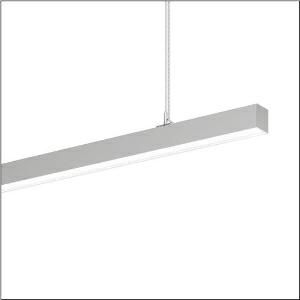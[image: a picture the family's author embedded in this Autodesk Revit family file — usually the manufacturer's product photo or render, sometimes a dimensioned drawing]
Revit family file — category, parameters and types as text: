
# Revit family: silica_r__21_51mx33da37sb_bea4
name_source: partatom
category: Lighting Fixtures
units: mm (PartAtom-declared; Revit-internal decimal feet)

## family parameters
Cut with Voids When Loaded = No
Host = Face
Light Source = No
Part Type = Normal
Room Calculation Point = No
Round Connector Dimension = Use Diameter
Shared = No

## types (1)
- --- (1 x LED, 5910 lm, 41.3 W, 3000K)
    Apparent Load = 41 VA
    CIE Flux Codes = 78 96 99 55 100
    Color Rendering = 80
    Color Temperature = 3000K
    Default Elevation = 1800 mm
    Description = Silica® 21, office luminaire, primary optical cover: prismatic diffuser, of PMMA, CAT 2 (L<= 3000cd/m²), light emission: direct/indirect distribution, primary light characteristic: symmetric, installation type: suspended mounting, LED, rated luminous flux: 5.910lm, luminous efficacy: 143lm/W, light colour: 830, colour temperature: 3000K, with terminal, 3+2-pole, max. 2.5mm², mains connection: 220..240V, AC, 50/60Hz, rated input power: 41.3W, luminaire housing, of aluminium, metallic grey (RAL 9006), length: 1.204mm, width: 53mm, height: 53mm, protection rating (complete): IP20, insulation class (complete): insulation class I (protective earthing), certification: CE, permissible operating ambient temperature: 0..+35°C, standard: EN 50419, packaging unit: 1 piece
    Height = 53 mm
    Lamp = 1 x LED
    Lamp Light Flux = 5910 lm
    Lamp Power = 41.3 W
    Lamp count = 1
    Length = 1204 mm
    Luminous efficacy = 143 lm/W
    Manufacturer = Siteco
    ModVariant = No
    Model = 51MX33DA37SB
    Mounting Place = Ceiling
    Mounting Type = Pendant
    Number of Poles = 1
    OnlyDefault = Yes
    Power Factor = 1
    Product Name = Silica® 21
    Product group = office luminaire | ceiling pendant
    ProductGroupID = 902
    Protection Class = Protection class I
    Protection Degree = IP 20
    RLX_Detail_Level = 1
    RLX_Emergency_Light_Flux = 0 lm
    RLX_Emergency_Type = 0
    RLX_Emergency_Type_DB = No
    RlxData = <blob elided: 23281 chars, md5=2ed932aa>
    Socket = socket
    Standby Power = 0 W
    System Light Flux = 5910 lm
    System Power = 41 W
    Type Comments = factory setting: luminous flux: 100 % | dim-lin: 254 | 345 mA
    Type Image = l_1335864.jpg
    URL = http://relux.com
    VarID = @adj_087713
    Voltage = 0 V
    Weight = 0.00 kg
    Width = 53 mm

## geometry (parser evidence)
native form markers: Blend x4, Sweep x12
no freeform markers — native parametric forms only
